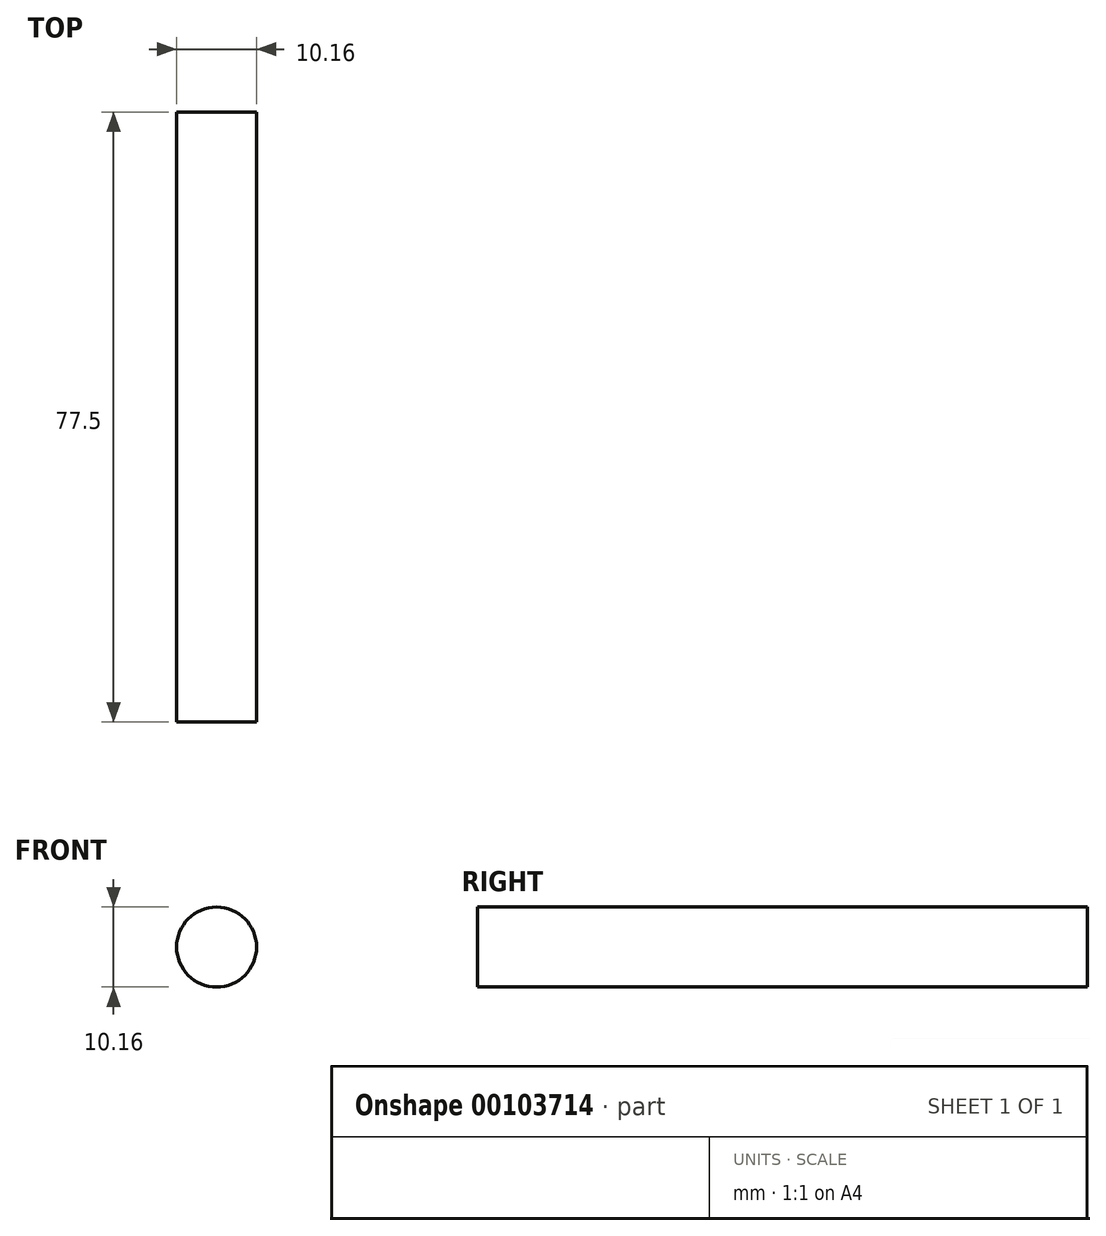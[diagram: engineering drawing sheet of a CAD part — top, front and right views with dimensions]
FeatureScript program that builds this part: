
annotation { "Feature Type Name" : "Feature", "Feature Type Description" : "" }
export const myFeature = defineFeature(function(context is Context, id is Id, definition is map)
    precondition{}
    {
        {
            var Q0;
            Q0=qCreatedBy(makeId("Front.planeOp"),FACE);
            var sketch = newSketch(context, id + "F0", { "sketchPlane" : qUnion([Q0])});
            skCircle(sketch, "E0", {"center": v(0, 0) * mm, "radius": 5.08 * mm});
            skSolve(sketch);
        }
        {
            var Q0;
            Q0=makeQuery(id+"F0.imprint","IMPRINT",FACE,{"disambiguationData":[TD([[makeQuery(id+"F0.imprint","IMPRINT",EDGE,{"derivedFrom":sQuery(id+"F0.wireOp",EDGE,"E0")}),1.0]])]});
            extrude(context, id + "F1", {"entities" : qUnion([Q0]), "endBound" : BoundingType.SYMMETRIC, "depth" : 77.5 * mm});
        }
    });
